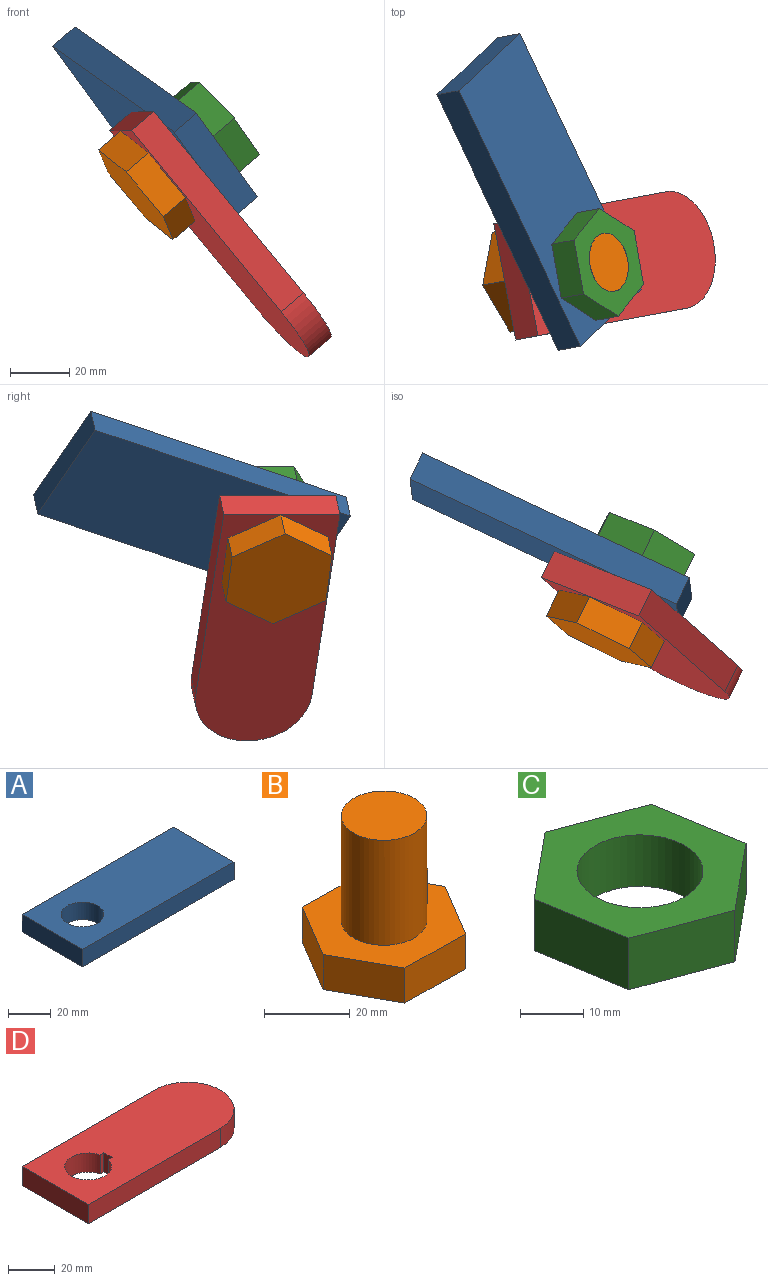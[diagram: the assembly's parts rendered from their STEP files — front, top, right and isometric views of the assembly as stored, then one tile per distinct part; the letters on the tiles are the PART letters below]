
ASSEMBLY  parts=4 mates=3
PART A: 7 faces, bbox 100x40x10 mm
  f0: plane 100x10mm, normal (0,-1,0), area 1000mm2, adj f1,f4,f5,f6
  f1: plane 40x10mm, normal (1,0,0), area 400mm2, adj f0,f2,f5,f6
  f2: plane 100x10mm, normal (0,1,0), area 1000mm2, adj f1,f4,f5,f6
  f3: cylinder r=10mm len=20mm, axis (0,0,-1), area 628.3mm2, adj f5,f6
  f4: plane 40x10mm, normal (-1,0,0), area 400mm2, adj f0,f2,f5,f6
  f5: plane 100x40mm, normal (0,0,1), area 3685.8mm2, adj f0,f1,f2,f3,f4
  f6: plane 100x40mm, normal (0,0,-1), area 3685.8mm2, adj f0,f1,f2,f3,f4
PART B: 14 faces, bbox 39.6x34.6x40 mm
  f0: cylinder r=10mm len=30mm, axis (0,0,-1), area 1834.4mm2, adj f1,f2,f3,f5,f6
  f1: plane 20x20mm, normal (0,0,1), area 314.2mm2, adj f0
  f2: plane 10x2.32mm, normal (0,1,0), area 23.2mm2, adj f0,f4,f5,f6
  f3: plane 10x2.32mm, normal (0,-1,0), area 23.2mm2, adj f0,f4,f5,f6
  f4: plane 10x5mm, normal (1,0,0), area 50mm2, adj f2,f3,f5,f6
  f5: plane 5x2.32mm, normal (0,0,1), area 10.5mm2, adj f0,f2,f3,f4
  f6: plane 39.63x34.64mm, normal (0,0,1), area 695.9mm2, adj f0,f2,f3,f4,f7,f8,f9,f10
  f7: plane 17.32x10mm, normal (-0.87,-0.49,0), area 198.2mm2, adj f6,f8,f12,f13
  f8: plane 19.82x10mm, normal (-0.02,-1,0), area 198.2mm2, adj f6,f7,f9,f13
  f9: plane 17x10.18mm, normal (0.86,-0.51,0), area 198.2mm2, adj f6,f8,f10,f13
  f10: plane 17.32x10mm, normal (0.87,0.49,0), area 198.2mm2, adj f6,f9,f11,f13
  f11: plane 19.82x10mm, normal (0.02,1,0), area 198.2mm2, adj f6,f10,f12,f13
  f12: plane 17x10.18mm, normal (-0.86,0.51,0), area 198.2mm2, adj f6,f7,f11,f13
  f13: plane 39.63x34.64mm, normal (0,0,-1), area 1020.6mm2, adj f7,f8,f9,f10,f11,f12
PART C: 9 faces, bbox 34.6x36.5x10 mm
  f0: plane 18.24x10mm, normal (-0.99,-0.17,0), area 184.9mm2, adj f1,f6,f7,f8
  f1: plane 17.32x10mm, normal (-0.35,-0.94,0), area 184.9mm2, adj f0,f2,f7,f8
  f2: plane 14.26x11.76mm, normal (0.64,-0.77,0), area 184.9mm2, adj f1,f3,f7,f8
  f3: plane 18.24x10mm, normal (0.99,0.17,0), area 184.9mm2, adj f2,f4,f7,f8
  f4: plane 17.32x10mm, normal (0.35,0.94,0), area 184.9mm2, adj f3,f6,f7,f8
  f5: cylinder r=10mm len=20mm, axis (0,0,1), area 628.3mm2, adj f7,f8
  f6: plane 14.26x11.76mm, normal (-0.64,0.77,0), area 184.9mm2, adj f0,f4,f7,f8
  f7: plane 36.47x34.64mm, normal (0,0,-1), area 574.1mm2, adj f0,f1,f2,f3,f4,f5,f6
  f8: plane 36.47x34.64mm, normal (0,0,1), area 574.1mm2, adj f0,f1,f2,f3,f4,f5,f6
PART D: 10 faces, bbox 100x40x10 mm
  f0: plane 80x10mm, normal (0,-1,0), area 800mm2, adj f1,f7,f8,f9
  f1: cylinder r=20mm len=40mm, axis (0,0,1), area 628.3mm2, adj f0,f2,f8,f9
  f2: plane 80x10mm, normal (0,1,0), area 800mm2, adj f1,f7,f8,f9
  f3: plane 10x5mm, normal (-1,0,0), area 50mm2, adj f4,f6,f8,f9
  f4: plane 10x2.32mm, normal (0,1,0), area 23.2mm2, adj f3,f5,f8,f9
  f5: cylinder r=10mm len=20mm, axis (0,0,1), area 577.8mm2, adj f4,f6,f8,f9
  f6: plane 10x2.32mm, normal (0,-1,0), area 23.2mm2, adj f3,f5,f8,f9
  f7: plane 40x10mm, normal (-1,0,0), area 400mm2, adj f0,f2,f8,f9
  f8: plane 100x40mm, normal (0,0,-1), area 3503.6mm2, adj f0,f1,f2,f3,f4,f5,f6,f7
  f9: plane 100x40mm, normal (0,0,1), area 3503.6mm2, adj f0,f1,f2,f3,f4,f5,f6,f7
PLACE A rot(axis=(0.36,0.3,0.88),128.7deg) t=(-54.28,5.42,3.02)mm
PLACE B rot(axis=(-0.09,0.98,0.19),51deg) t=(-80.3,11.62,16.58)mm
PLACE C rot(axis=(-0.18,0.98,0),50deg) t=(-57.72,15.87,35.87)mm
PLACE D rot(axis=(-0.09,0.98,0.19),51deg) t=(-81.72,-8.99,38.33)mm
MATE revolute B.f0 <-> C.f5  axis (0.75,0.14,0.64) through (-57.72,15.87,35.87)mm
MATE revolute A.f3 <-> D.f5  axis (-0.75,-0.14,-0.64) through (-72.78,13.04,23.01)mm
MATE fastened B.f4 <-> D.f3  axis (0.63,0.12,-0.77) through (-68.96,13.75,10.6)mm
